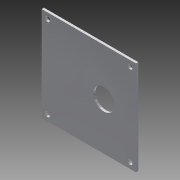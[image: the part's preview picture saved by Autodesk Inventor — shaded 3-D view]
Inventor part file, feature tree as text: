
AUTODESK INVENTOR PART (.ipt)
format: ipt  version: 2015 (Build 190159000, 159)  size: 113,664 bytes
history: native  units: in
note: dims shown in document units (in); Inventor stores cm internally (conversion verified against a paired STEP export)
features: other x3, hole x2, sketch x1
ambient origin geometry x8: Origin, YZ Plane, XZ Plane, XY Plane, X Axis, Y Axis, Z Axis, Center Point
bodies: Solid1 (feature_tree)
feature tree (6):
  hole  "gbmh"  [1 undecoded]
  hole  "ss_bearing_hole"  [1 undecoded]
  sketch  "Sketch1"  dims[d0=5.0in d1=0.12in d2=4.376in d3=4.376in d4=4.376in d5=4.376in d6=0.25in d7=0.75in d8=0.375in d9=0.25in d10=0.5635in d11=0.12in d12=0.8108in d13=1.5in d14=1.5in d15=1.125in d16=0.75in d17=0.375in d18=0.25in d19=0.5635in d20=0.12in d21=0.8108in]
  other  "Plate1"
  other  "gbmh_sketch"
  other  "bearing_hole_sketch"
note: 2 required parameter values undecoded (feature->parameter linkage not recoverable at this tier; creation-order binding heuristic only, values carry confidence <= 0.55)
